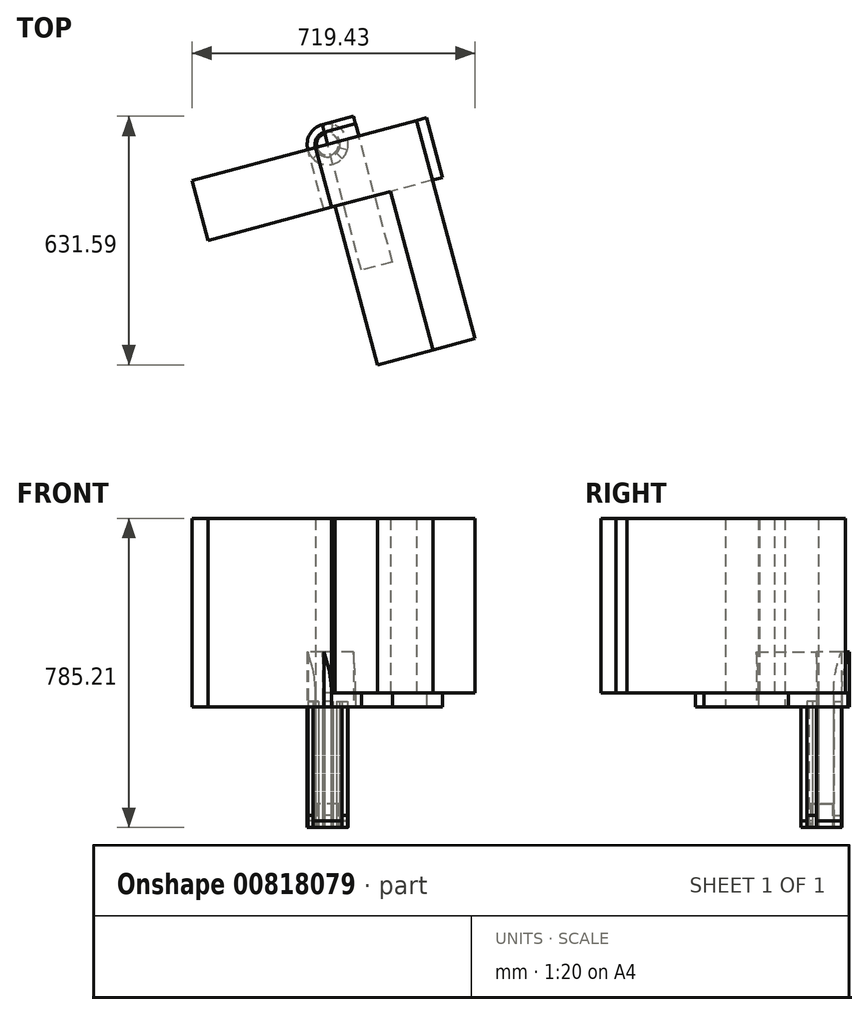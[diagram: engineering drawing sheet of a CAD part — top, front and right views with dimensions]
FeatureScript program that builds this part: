
annotation { "Feature Type Name" : "Feature", "Feature Type Description" : "" }
export const myFeature = defineFeature(function(context is Context, id is Id, definition is map)
    precondition{}
    {
        {
            var Q0;
            Q0=qCreatedBy(makeId("Top.planeOp"),FACE);
            var sketch = newSketch(context, id + "F0", { "sketchPlane" : qUnion([Q0])});
            skCircle(sketch, "E0", {"center": v(0, 0) * mm, "radius": 52 * mm});
            skCircle(sketch, "E1", {"center": v(0, 0) * mm, "radius": 28 * mm});
            skCircle(sketch, "E2", {"center": v(0, 0) * mm, "radius": 32 * mm});
            skLineSegment(sketch, "E3", {"start": v(0, 0) * mm, "end": v(0, 80.06) * mm});
            skLineSegment(sketch, "E4", {"start": v(0, -28) * mm, "end": v(0, -32) * mm});
            skLineSegment(sketch, "E5", {"start": v(0, 0) * mm, "end": v(-81.12, -46.83) * mm});
            skLineSegment(sketch, "E6", {"start": v(0, 0) * mm, "end": v(68.65, -39.63) * mm});
            skLineSegment(sketch, "E7", {"start": v(0, 0) * mm, "end": v(21.03, 78.5) * mm});
            skLineSegment(sketch, "E8", {"start": v(0, 0) * mm, "end": v(-20.05, 74.83) * mm});
            skLineSegment(sketch, "E9", {"start": v(0, 0) * mm, "end": v(-94.25, -25.26) * mm});
            skLineSegment(sketch, "E10", {"start": v(0, 0) * mm, "end": v(-57.02, -57.02) * mm});
            skLineSegment(sketch, "E11", {"start": v(0, 0) * mm, "end": v(53.16, -53.16) * mm});
            skLineSegment(sketch, "E12", {"start": v(0, 0) * mm, "end": v(77.92, -20.88) * mm});
            skSolve(sketch);
        }
        {
            var Q0;
            {var subQ0=sQuery(id+"F0.wireOp",EDGE,"E3");var subQ1=sQuery(id+"F0.wireOp",EDGE,"E0");var subQ2=makeQuery(id+"F0.imprint","INTERSECT",VERTEX,{"derivedFrom":[subQ1,subQ0]});Q0=makeQuery(id+"F0.imprint","IMPRINT",FACE,{"disambiguationData":[TD([[makeQuery(id+"F0.imprint","IMPRINT",EDGE,{"disambiguationData":[TD([[subQ2,1.0]])],"derivedFrom":subQ1}),1.0]])]});}
            var Q1;
            {var subQ0=sQuery(id+"F0.wireOp",EDGE,"E3");var subQ1=sQuery(id+"F0.wireOp",EDGE,"E0");var subQ2=makeQuery(id+"F0.imprint","INTERSECT",VERTEX,{"derivedFrom":[subQ1,subQ0]});Q1=makeQuery(id+"F0.imprint","IMPRINT",FACE,{"disambiguationData":[TD([[makeQuery(id+"F0.imprint","IMPRINT",EDGE,{"disambiguationData":[TD([[subQ2,-1.0]])],"derivedFrom":subQ1}),1.0]])]});}
            extrude(context, id + "F1", {"entities" : qUnion([Q0, Q1]), "depth" : 14 * mm, "offsetDistance" : 25 * mm});
        }
        {
            var Q0;
            {var subQ0=sQuery(id+"F0.wireOp",EDGE,"E9");var subQ1=sQuery(id+"F0.wireOp",EDGE,"E0");var subQ2=makeQuery(id+"F0.imprint","INTERSECT",VERTEX,{"derivedFrom":[subQ1,subQ0]});Q0=makeQuery(id+"F0.imprint","IMPRINT",FACE,{"disambiguationData":[TD([[makeQuery(id+"F0.imprint","IMPRINT",EDGE,{"disambiguationData":[TD([[subQ2,-1.0]])],"derivedFrom":subQ1}),1.0]])]});}
            var Q1;
            {var subQ0=sQuery(id+"F0.wireOp",EDGE,"E5");var subQ1=sQuery(id+"F0.wireOp",EDGE,"E0");var subQ2=makeQuery(id+"F0.imprint","INTERSECT",VERTEX,{"derivedFrom":[subQ1,subQ0]});Q1=makeQuery(id+"F0.imprint","IMPRINT",FACE,{"disambiguationData":[TD([[makeQuery(id+"F0.imprint","IMPRINT",EDGE,{"disambiguationData":[TD([[subQ2,-1.0]])],"derivedFrom":subQ1}),1.0]])]});}
            var Q2;
            {var subQ0=sQuery(id+"F0.wireOp",EDGE,"E3");var subQ1=sQuery(id+"F0.wireOp",EDGE,"E0");var subQ2=makeQuery(id+"F0.imprint","INTERSECT",VERTEX,{"derivedFrom":[subQ1,subQ0]});Q2=makeQuery(id+"F0.imprint","IMPRINT",FACE,{"disambiguationData":[TD([[makeQuery(id+"F0.imprint","IMPRINT",EDGE,{"disambiguationData":[TD([[subQ2,-1.0]])],"derivedFrom":subQ1}),1.0]])]});}
            var Q3;
            {var subQ0=sQuery(id+"F0.wireOp",EDGE,"E3");var subQ1=sQuery(id+"F0.wireOp",EDGE,"E0");var subQ2=makeQuery(id+"F0.imprint","INTERSECT",VERTEX,{"derivedFrom":[subQ1,subQ0]});Q3=makeQuery(id+"F0.imprint","IMPRINT",FACE,{"disambiguationData":[TD([[makeQuery(id+"F0.imprint","IMPRINT",EDGE,{"disambiguationData":[TD([[subQ2,1.0]])],"derivedFrom":subQ1}),1.0]])]});}
            var Q4;
            {var subQ0=sQuery(id+"F0.wireOp",EDGE,"E6");var subQ1=sQuery(id+"F0.wireOp",EDGE,"E0");var subQ2=makeQuery(id+"F0.imprint","INTERSECT",VERTEX,{"derivedFrom":[subQ1,subQ0]});Q4=makeQuery(id+"F0.imprint","IMPRINT",FACE,{"disambiguationData":[TD([[makeQuery(id+"F0.imprint","IMPRINT",EDGE,{"disambiguationData":[TD([[subQ2,-1.0]])],"derivedFrom":subQ1}),1.0]])]});}
            var Q5;
            {var subQ0=sQuery(id+"F0.wireOp",EDGE,"E11");var subQ1=sQuery(id+"F0.wireOp",EDGE,"E0");var subQ2=makeQuery(id+"F0.imprint","INTERSECT",VERTEX,{"derivedFrom":[subQ1,subQ0]});Q5=makeQuery(id+"F0.imprint","IMPRINT",FACE,{"disambiguationData":[TD([[makeQuery(id+"F0.imprint","IMPRINT",EDGE,{"disambiguationData":[TD([[subQ2,-1.0]])],"derivedFrom":subQ1}),1.0]])]});}
            extrude(context, id + "F2", {"entities" : qUnion([Q0, Q1, Q2, Q3, Q4, Q5]), "operationType" : NewBodyOperationType.ADD, "depth" : 30 * mm, "offsetDistance" : 25 * mm});
        }
        {
            var Q0;
            {var subQ0=sQuery(id+"F0.wireOp",EDGE,"E8");var subQ1=sQuery(id+"F0.wireOp",EDGE,"E0");var subQ2=makeQuery(id+"F0.imprint","INTERSECT",VERTEX,{"derivedFrom":[subQ1,subQ0]});Q0=makeQuery(id+"F0.imprint","IMPRINT",FACE,{"disambiguationData":[TD([[makeQuery(id+"F0.imprint","IMPRINT",EDGE,{"disambiguationData":[TD([[subQ2,-1.0]])],"derivedFrom":subQ1}),1.0]])]});}
            var Q1;
            {var subQ0=sQuery(id+"F0.wireOp",EDGE,"E7");var subQ1=sQuery(id+"F0.wireOp",EDGE,"E0");var subQ2=makeQuery(id+"F0.imprint","INTERSECT",VERTEX,{"derivedFrom":[subQ1,subQ0]});Q1=makeQuery(id+"F0.imprint","IMPRINT",FACE,{"disambiguationData":[TD([[makeQuery(id+"F0.imprint","IMPRINT",EDGE,{"disambiguationData":[TD([[subQ2,1.0]])],"derivedFrom":subQ1}),1.0]])]});}
            var Q2;
            {var subQ2=sQuery(id+"F0.wireOp",EDGE,"E10");var subQ4=sQuery(id+"F0.wireOp",EDGE,"E0");var subQ5=makeQuery(id+"F0.imprint","INTERSECT",VERTEX,{"derivedFrom":[subQ4,subQ2]});Q2=makeQuery(id+"F0.imprint","IMPRINT",FACE,{"disambiguationData":[TD([[makeQuery(id+"F0.imprint","IMPRINT",EDGE,{"disambiguationData":[TD([[subQ5,-1.0]])],"derivedFrom":subQ4}),1.0]])]});}
            extrude(context, id + "F3", {"entities" : qUnion([Q0, Q1, Q2]), "depth" : 16 * mm, "offsetDistance" : 25 * mm});
        }
        {
            var Q0;
            {var subQ0=sQuery(id+"F0.wireOp",EDGE,"E1");var subQ1=makeQuery(id+"F0.imprint","INTERSECT",VERTEX,{"derivedFrom":[subQ0,sQuery(id+"F0.wireOp",EDGE,"E4")]});Q0=makeQuery(id+"F0.imprint","IMPRINT",FACE,{"disambiguationData":[TD([[makeQuery(id+"F0.imprint","IMPRINT",EDGE,{"disambiguationData":[TD([[subQ1,1.0]])],"derivedFrom":subQ0}),1.0]])]});}
            var Q1;
            {var subQ0=sQuery(id+"F0.wireOp",EDGE,"E8");var subQ1=sQuery(id+"F0.wireOp",EDGE,"E1");var subQ2=makeQuery(id+"F0.imprint","INTERSECT",VERTEX,{"derivedFrom":[subQ1,subQ0]});Q1=makeQuery(id+"F0.imprint","IMPRINT",FACE,{"disambiguationData":[TD([[makeQuery(id+"F0.imprint","IMPRINT",EDGE,{"disambiguationData":[TD([[subQ2,-1.0]])],"derivedFrom":subQ1}),1.0]])]});}
            var Q2;
            {var subQ0=sQuery(id+"F0.wireOp",EDGE,"E7");var subQ1=sQuery(id+"F0.wireOp",EDGE,"E1");var subQ2=makeQuery(id+"F0.imprint","INTERSECT",VERTEX,{"derivedFrom":[subQ1,subQ0]});Q2=makeQuery(id+"F0.imprint","IMPRINT",FACE,{"disambiguationData":[TD([[makeQuery(id+"F0.imprint","IMPRINT",EDGE,{"disambiguationData":[TD([[subQ2,1.0]])],"derivedFrom":subQ1}),1.0]])]});}
            var Q3;
            {var subQ0=sQuery(id+"F0.wireOp",EDGE,"E6");var subQ1=sQuery(id+"F0.wireOp",EDGE,"E1");var subQ2=makeQuery(id+"F0.imprint","INTERSECT",VERTEX,{"derivedFrom":[subQ1,subQ0]});Q3=makeQuery(id+"F0.imprint","IMPRINT",FACE,{"disambiguationData":[TD([[makeQuery(id+"F0.imprint","IMPRINT",EDGE,{"disambiguationData":[TD([[subQ2,-1.0]])],"derivedFrom":subQ1}),1.0]])]});}
            var Q4;
            {var subQ0=sQuery(id+"F0.wireOp",EDGE,"E11");var subQ1=sQuery(id+"F0.wireOp",EDGE,"E1");var subQ2=makeQuery(id+"F0.imprint","INTERSECT",VERTEX,{"derivedFrom":[subQ1,subQ0]});Q4=makeQuery(id+"F0.imprint","IMPRINT",FACE,{"disambiguationData":[TD([[makeQuery(id+"F0.imprint","IMPRINT",EDGE,{"disambiguationData":[TD([[subQ2,-1.0]])],"derivedFrom":subQ1}),1.0]])]});}
            var Q5;
            {var subQ0=sQuery(id+"F0.wireOp",EDGE,"E3");var subQ1=sQuery(id+"F0.wireOp",EDGE,"E1");var subQ2=makeQuery(id+"F0.imprint","INTERSECT",VERTEX,{"derivedFrom":[subQ1,subQ0]});Q5=makeQuery(id+"F0.imprint","IMPRINT",FACE,{"disambiguationData":[TD([[makeQuery(id+"F0.imprint","IMPRINT",EDGE,{"disambiguationData":[TD([[subQ2,1.0]])],"derivedFrom":subQ1}),1.0]])]});}
            var Q6;
            {var subQ0=sQuery(id+"F0.wireOp",EDGE,"E3");var subQ1=sQuery(id+"F0.wireOp",EDGE,"E1");var subQ2=makeQuery(id+"F0.imprint","INTERSECT",VERTEX,{"derivedFrom":[subQ1,subQ0]});Q6=makeQuery(id+"F0.imprint","IMPRINT",FACE,{"disambiguationData":[TD([[makeQuery(id+"F0.imprint","IMPRINT",EDGE,{"disambiguationData":[TD([[subQ2,-1.0]])],"derivedFrom":subQ1}),1.0]])]});}
            var Q7;
            {var subQ0=sQuery(id+"F0.wireOp",EDGE,"E9");var subQ1=sQuery(id+"F0.wireOp",EDGE,"E1");var subQ2=makeQuery(id+"F0.imprint","INTERSECT",VERTEX,{"derivedFrom":[subQ1,subQ0]});Q7=makeQuery(id+"F0.imprint","IMPRINT",FACE,{"disambiguationData":[TD([[makeQuery(id+"F0.imprint","IMPRINT",EDGE,{"disambiguationData":[TD([[subQ2,-1.0]])],"derivedFrom":subQ1}),1.0]])]});}
            var Q8;
            {var subQ0=sQuery(id+"F0.wireOp",EDGE,"E5");var subQ1=sQuery(id+"F0.wireOp",EDGE,"E1");var subQ2=makeQuery(id+"F0.imprint","INTERSECT",VERTEX,{"derivedFrom":[subQ1,subQ0]});Q8=makeQuery(id+"F0.imprint","IMPRINT",FACE,{"disambiguationData":[TD([[makeQuery(id+"F0.imprint","IMPRINT",EDGE,{"disambiguationData":[TD([[subQ2,-1.0]])],"derivedFrom":subQ1}),1.0]])]});}
            extrude(context, id + "F4", {"entities" : qUnion([Q0, Q1, Q2, Q3, Q4, Q5, Q6, Q7, Q8]), "depth" : 59 * mm, "offsetDistance" : 25 * mm});
        }
        {
            var Q0;
            Q0=makeQuery(id+"F3.opExtrude","CAP_FACE",FACE,{"disambiguationData":[OSD([sQuery(id+"F0.wireOp",EDGE,"E0"),sQuery(id+"F0.wireOp",EDGE,"E2"),sQuery(id+"F0.wireOp",EDGE,"E8"),sQuery(id+"F0.wireOp",EDGE,"E9")])],"isStart":false});
            var Q1;
            Q1=makeQuery(id+"F3.opExtrude","CAP_FACE",FACE,{"disambiguationData":[OSD([sQuery(id+"F0.wireOp",EDGE,"E0"),sQuery(id+"F0.wireOp",EDGE,"E2"),sQuery(id+"F0.wireOp",EDGE,"E7"),sQuery(id+"F0.wireOp",EDGE,"E12")])],"isStart":false});
            var Q2;
            Q2=makeQuery(id+"F3.opExtrude","CAP_FACE",FACE,{"disambiguationData":[OSD([sQuery(id+"F0.wireOp",EDGE,"E0"),sQuery(id+"F0.wireOp",EDGE,"E2"),sQuery(id+"F0.wireOp",EDGE,"E10"),sQuery(id+"F0.wireOp",EDGE,"E11")])],"isStart":false});
            var Q3;
            Q3=makeQuery(id+"F2.opExtrude","CAP_FACE",FACE,{"disambiguationData":[OSD([sQuery(id+"F0.wireOp",EDGE,"E0"),sQuery(id+"F0.wireOp",EDGE,"E2"),sQuery(id+"F0.wireOp",EDGE,"E9"),sQuery(id+"F0.wireOp",EDGE,"E10")])],"isStart":false});
            var Q4;
            Q4=makeQuery(id+"F2.opExtrude","CAP_FACE",FACE,{"disambiguationData":[OSD([sQuery(id+"F0.wireOp",EDGE,"E0"),sQuery(id+"F0.wireOp",EDGE,"E2"),sQuery(id+"F0.wireOp",EDGE,"E7"),sQuery(id+"F0.wireOp",EDGE,"E8")])],"isStart":false});
            var Q5;
            Q5=makeQuery(id+"F2.opExtrude","CAP_FACE",FACE,{"disambiguationData":[OSD([sQuery(id+"F0.wireOp",EDGE,"E0"),sQuery(id+"F0.wireOp",EDGE,"E2"),sQuery(id+"F0.wireOp",EDGE,"E11"),sQuery(id+"F0.wireOp",EDGE,"E12")])],"isStart":false});
            extrude(context, id + "F5", {"entities" : qUnion([Q0, Q1, Q2, Q3, Q4, Q5]), "depth" : 290 * mm, "offsetDistance" : 25 * mm});
        }
        {
            var Q0;
            Q0=makeQuery(id+"F5.opExtrude","CAP_FACE",FACE,{"disambiguationData":[OSD([sQuery(id+"F0.wireOp",EDGE,"E0"),sQuery(id+"F0.wireOp",EDGE,"E2"),sQuery(id+"F0.wireOp",EDGE,"E8"),sQuery(id+"F0.wireOp",EDGE,"E9")])],"isStart":false});
            extrude(context, id + "F6", {"entities" : qUnion([Q0]), "depth" : 139 * mm, "offsetDistance" : 25 * mm});
        }
        {
            var Q0;
            Q0=makeQuery(id+"F6.opExtrude","CAP_EDGE",EDGE,{"disambiguationData":[OSD([sQuery(id+"F0.wireOp",EDGE,"E2")])],"isStart":false});
            fillet(context, id + "F7", {"entities" : qUnion([Q0]), "radius" : 279.32 * mm, "tangentPropagation" : true, "allowEdgeOverflow" : false});
        }
        {
            var Q0;
            Q0=makeQuery(id+"F6.opExtrude","SWEPT_FACE",FACE,{"disambiguationData":[OSD([sQuery(id+"F0.wireOp",EDGE,"E9")])]});
            extrude(context, id + "F8", {"entities" : qUnion([Q0]), "depth" : 157 * mm, "offsetDistance" : 25 * mm});
        }
        {
            var Q0;
            Q0=makeQuery(id+"F6.opExtrude","SWEPT_FACE",FACE,{"disambiguationData":[OSD([sQuery(id+"F0.wireOp",EDGE,"E8")])]});
            extrude(context, id + "F9", {"entities" : qUnion([Q0]), "depth" : 82 * mm, "offsetDistance" : 25 * mm});
        }
        {
            var Q0;
            {var subQ0=sQuery(id+"F0.wireOp",EDGE,"E9");var subQ1=sQuery(id+"F0.wireOp",EDGE,"E2");Q0=makeQuery(id+"F8.opExtrude","SWEPT_FACE",FACE,{"disambiguationData":[OSD([subQ1,subQ0]),TDD([makeQuery(id+"F6.opExtrude","SWEPT_EDGE",EDGE,{"disambiguationData":[OSD([subQ1,subQ0])]})])]});}
            extrude(context, id + "F10", {"entities" : qUnion([Q0]), "depth" : 155 * mm, "offsetDistance" : 25 * mm});
        }
        {
            var Q0;
            {var subQ0=sQuery(id+"F0.wireOp",EDGE,"E8");var subQ1=sQuery(id+"F0.wireOp",EDGE,"E2");Q0=makeQuery(id+"F9.opExtrude","SWEPT_FACE",FACE,{"disambiguationData":[OSD([subQ1,subQ0]),TDD([makeQuery(id+"F6.opExtrude","SWEPT_EDGE",EDGE,{"disambiguationData":[OSD([subQ1,subQ0])]})])]});}
            extrude(context, id + "F11", {"entities" : qUnion([Q0]), "depth" : 232 * mm, "offsetDistance" : 25 * mm});
        }
        {
            var Q0;
            {var subQ0=sQuery(id+"F0.wireOp",EDGE,"E9");var subQ1=sQuery(id+"F0.wireOp",EDGE,"E2");Q0=makeQuery(id+"F10.opExtrude","SWEPT_FACE",FACE,{"disambiguationData":[OSD([subQ1,subQ0]),TDD([makeQuery(id+"F8.opExtrude","SWEPT_EDGE",EDGE,{"disambiguationData":[OSD([subQ1,subQ0]),TDD([makeQuery(id+"F7.opFillet","BLEND_VERTEX",VERTEX,{"blendedFrom":[makeQuery(id+"F6.opExtrude","CAP_EDGE",EDGE,{"disambiguationData":[OSD([subQ1])],"isStart":false}),makeQuery(id+"F6.opExtrude","SWEPT_FACE",FACE,{"disambiguationData":[OSD([subQ1])]}),makeQuery(id+"F6.opExtrude","SWEPT_FACE",FACE,{"disambiguationData":[OSD([subQ0])]})],"blendedInto":[makeQuery(id+"F6.opExtrude","SWEPT_FACE",FACE,{"disambiguationData":[OSD([subQ1])]}),makeQuery(id+"F6.opExtrude","SWEPT_FACE",FACE,{"disambiguationData":[OSD([subQ0])]})]})])]})])]});}
            extrude(context, id + "F12", {"entities" : qUnion([Q0]), "depth" : 444 * mm, "offsetDistance" : 25 * mm});
        }
        {
            var Q0;
            Q0=makeQuery(id+"F10.opExtrude","CAP_FACE",FACE,{"disambiguationData":[OSD([sQuery(id+"F0.wireOp",EDGE,"E2"),sQuery(id+"F0.wireOp",EDGE,"E9")])],"isStart":false});
            extrude(context, id + "F13", {"entities" : qUnion([Q0]), "operationType" : NewBodyOperationType.ADD, "depth" : 137 * mm, "offsetDistance" : 25 * mm});
        }
        {
            var Q0;
            Q0=makeQuery(id+"F11.opExtrude","CAP_FACE",FACE,{"disambiguationData":[OSD([sQuery(id+"F0.wireOp",EDGE,"E2"),sQuery(id+"F0.wireOp",EDGE,"E8")])],"isStart":false});
            extrude(context, id + "F14", {"entities" : qUnion([Q0]), "operationType" : NewBodyOperationType.ADD, "depth" : 131 * mm, "offsetDistance" : 25 * mm});
        }
        {
            var Q0;
            {var subQ0=sQuery(id+"F0.wireOp",EDGE,"E9");var subQ1=sQuery(id+"F0.wireOp",EDGE,"E2");Q0=makeQuery(id+"F12.opExtrude","SWEPT_FACE",FACE,{"disambiguationData":[OSD([subQ1,subQ0]),TDD([makeQuery(id+"F10.opExtrude","CAP_EDGE",EDGE,{"disambiguationData":[OSD([subQ1,subQ0]),TDD([makeQuery(id+"F8.opExtrude","SWEPT_EDGE",EDGE,{"disambiguationData":[OSD([subQ1,subQ0]),TDD([makeQuery(id+"F7.opFillet","BLEND_VERTEX",VERTEX,{"blendedFrom":[makeQuery(id+"F6.opExtrude","CAP_EDGE",EDGE,{"disambiguationData":[OSD([subQ1])],"isStart":false}),makeQuery(id+"F6.opExtrude","SWEPT_FACE",FACE,{"disambiguationData":[OSD([subQ1])]}),makeQuery(id+"F6.opExtrude","SWEPT_FACE",FACE,{"disambiguationData":[OSD([subQ0])]})],"blendedInto":[makeQuery(id+"F6.opExtrude","SWEPT_FACE",FACE,{"disambiguationData":[OSD([subQ1])]}),makeQuery(id+"F6.opExtrude","SWEPT_FACE",FACE,{"disambiguationData":[OSD([subQ0])]})]})])]})])],"isStart":false})])]});}
            extrude(context, id + "F15", {"entities" : qUnion([Q0]), "depth" : 111 * mm, "offsetDistance" : 25 * mm});
        }
        {
            var Q0;
            {var subQ0=sQuery(id+"F0.wireOp",EDGE,"E9");var subQ1=sQuery(id+"F0.wireOp",EDGE,"E2");Q0=makeQuery(id+"F15.opExtrude","SWEPT_FACE",FACE,{"disambiguationData":[OSD([subQ1,subQ0]),TDD([makeQuery(id+"F12.opExtrude","SWEPT_EDGE",EDGE,{"disambiguationData":[OSD([subQ1,subQ0]),TDD([makeQuery(id+"F10.opExtrude","CAP_VERTEX",VERTEX,{"disambiguationData":[OSD([subQ1,subQ0]),TDD([makeQuery(id+"F8.opExtrude","CAP_VERTEX",VERTEX,{"disambiguationData":[OSD([subQ1,subQ0]),TDD([makeQuery(id+"F7.opFillet","BLEND_VERTEX",VERTEX,{"blendedFrom":[makeQuery(id+"F6.opExtrude","CAP_EDGE",EDGE,{"disambiguationData":[OSD([subQ1])],"isStart":false}),makeQuery(id+"F6.opExtrude","SWEPT_FACE",FACE,{"disambiguationData":[OSD([subQ1])]}),makeQuery(id+"F6.opExtrude","SWEPT_FACE",FACE,{"disambiguationData":[OSD([subQ0])]})],"blendedInto":[makeQuery(id+"F6.opExtrude","SWEPT_FACE",FACE,{"disambiguationData":[OSD([subQ1])]}),makeQuery(id+"F6.opExtrude","SWEPT_FACE",FACE,{"disambiguationData":[OSD([subQ0])]})]})])],"isStart":false})])],"isStart":false})])]})])]});}
            extrude(context, id + "F16", {"entities" : qUnion([Q0]), "operationType" : NewBodyOperationType.ADD, "depth" : 359 * mm, "offsetDistance" : 25 * mm});
        }
        {
            var Q0;
            {var subQ0=sQuery(id+"F0.wireOp",EDGE,"E9");var subQ1=sQuery(id+"F0.wireOp",EDGE,"E2");Q0=makeQuery(id+"F12.opExtrude","SWEPT_FACE",FACE,{"disambiguationData":[OSD([subQ1,subQ0]),TDD([makeQuery(id+"F10.opExtrude","CAP_EDGE",EDGE,{"disambiguationData":[OSD([subQ1,subQ0]),TDD([makeQuery(id+"F8.opExtrude","SWEPT_EDGE",EDGE,{"disambiguationData":[OSD([subQ1,subQ0]),TDD([makeQuery(id+"F7.opFillet","BLEND_VERTEX",VERTEX,{"blendedFrom":[makeQuery(id+"F6.opExtrude","CAP_EDGE",EDGE,{"disambiguationData":[OSD([subQ1])],"isStart":false}),makeQuery(id+"F6.opExtrude","SWEPT_FACE",FACE,{"disambiguationData":[OSD([subQ1])]}),makeQuery(id+"F6.opExtrude","SWEPT_FACE",FACE,{"disambiguationData":[OSD([subQ0])]})],"blendedInto":[makeQuery(id+"F6.opExtrude","SWEPT_FACE",FACE,{"disambiguationData":[OSD([subQ1])]}),makeQuery(id+"F6.opExtrude","SWEPT_FACE",FACE,{"disambiguationData":[OSD([subQ0])]})]})])]})])],"isStart":true})])]});}
            extrude(context, id + "F17", {"entities" : qUnion([Q0]), "depth" : 325 * mm, "offsetDistance" : 25 * mm});
        }
        {
            var Q0;
            Q0=makeQuery(id+"F16.opExtrude","CAP_FACE",FACE,{"disambiguationData":[OSD([sQuery(id+"F0.wireOp",EDGE,"E2"),sQuery(id+"F0.wireOp",EDGE,"E9")])],"isStart":false});
            extrude(context, id + "F18", {"entities" : qUnion([Q0]), "operationType" : NewBodyOperationType.ADD, "depth" : 58 * mm, "offsetDistance" : 25 * mm});
        }
        {
            var Q0;
            {var subQ0=sQuery(id+"F0.wireOp",EDGE,"E9");var subQ1=sQuery(id+"F0.wireOp",EDGE,"E2");var subQ2=makeQuery(id+"F15.opExtrude","CAP_EDGE",EDGE,{"disambiguationData":[OSD([subQ1,subQ0]),TDD([makeQuery(id+"F12.opExtrude","SWEPT_EDGE",EDGE,{"disambiguationData":[OSD([subQ1,subQ0]),TDD([makeQuery(id+"F10.opExtrude","CAP_VERTEX",VERTEX,{"disambiguationData":[OSD([subQ1,subQ0]),TDD([makeQuery(id+"F8.opExtrude","CAP_VERTEX",VERTEX,{"disambiguationData":[OSD([subQ1,subQ0]),TDD([makeQuery(id+"F7.opFillet","BLEND_VERTEX",VERTEX,{"blendedFrom":[makeQuery(id+"F6.opExtrude","CAP_EDGE",EDGE,{"disambiguationData":[OSD([subQ1])],"isStart":false}),makeQuery(id+"F6.opExtrude","SWEPT_FACE",FACE,{"disambiguationData":[OSD([subQ1])]}),makeQuery(id+"F6.opExtrude","SWEPT_FACE",FACE,{"disambiguationData":[OSD([subQ0])]})],"blendedInto":[makeQuery(id+"F6.opExtrude","SWEPT_FACE",FACE,{"disambiguationData":[OSD([subQ1])]}),makeQuery(id+"F6.opExtrude","SWEPT_FACE",FACE,{"disambiguationData":[OSD([subQ0])]})]})])],"isStart":false})])],"isStart":false})])]})])],"isStart":true});Q0=makeQuery(id+"F18.boolean.opBoolean","MERGE",FACE,{"derivedFrom":[makeQuery(id+"F16.boolean.opBoolean","MERGE",FACE,{"derivedFrom":[makeQuery(id+"F15.opExtrude","CAP_FACE",FACE,{"disambiguationData":[OSD([subQ1,subQ0])],"isStart":true}),makeQuery(id+"F16.opExtrude","SWEPT_FACE",FACE,{"disambiguationData":[OSD([subQ1,subQ0]),TDD([subQ2])]})]}),makeQuery(id+"F18.opExtrude","SWEPT_FACE",FACE,{"disambiguationData":[OSD([subQ1,subQ0]),TDD([makeQuery(id+"F16.opExtrude","CAP_EDGE",EDGE,{"disambiguationData":[OSD([subQ1,subQ0]),TDD([subQ2])],"isStart":false})])]})]});}
            extrude(context, id + "F19", {"entities" : qUnion([Q0]), "depth" : 145 * mm, "offsetDistance" : 25 * mm});
        }
    });
